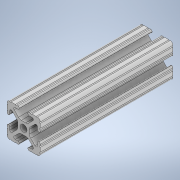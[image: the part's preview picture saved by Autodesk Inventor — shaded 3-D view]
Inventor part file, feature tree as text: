
AUTODESK INVENTOR PART (.ipt)
format: ipt  version: 2020 (Build 240168000, 168)  size: 236,032 bytes
history: native  units: in
note: dims shown in document units (in); Inventor stores cm internally (conversion verified against a paired STEP export)
features: extrude x1, sketch x1
ambient origin geometry x8: Origin, YZ Plane, XZ Plane, XY Plane, X Axis, Y Axis, Z Axis, Center Point
bodies: Solid1 (feature_tree)
feature tree (2):
  extrude  "Extrusion1"  [1 undecoded]
  sketch  "Sketch1"  dims[d0=4.0in d1=0.0in]
note: 1 required parameter value undecoded (feature->parameter linkage not recoverable at this tier; creation-order binding heuristic only, values carry confidence <= 0.55)
